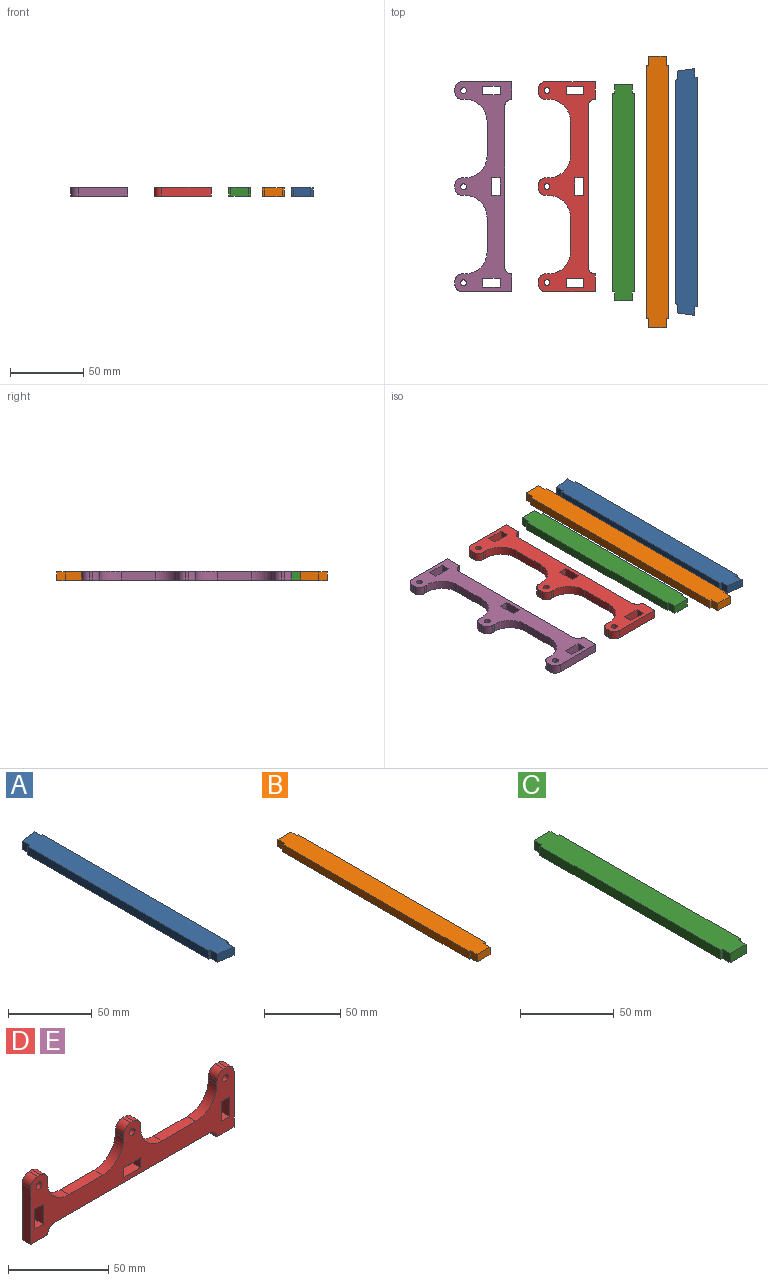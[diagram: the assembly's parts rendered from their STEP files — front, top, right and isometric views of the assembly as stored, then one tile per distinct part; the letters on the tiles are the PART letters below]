
ASSEMBLY  parts=5 mates=4
PART A: 14 faces, bbox 15x168.6x6 mm
  f0: plane 152.79x6mm, normal (-1,0,0), area 916.8mm2, adj f1,f11,f12,f13
  f1: plane 6x1.5mm, normal (-0.14,-0.99,0), area 9.1mm2, adj f0,f2,f12,f13
  f2: plane 6x6mm, normal (-1,0,0), area 36mm2, adj f1,f3,f12,f13
  f3: plane 12x6mm, normal (-0.14,-0.99,0), area 72.7mm2, adj f2,f4,f12,f13
  f4: plane 6x6mm, normal (1,0,0), area 36mm2, adj f3,f5,f12,f13
  f5: plane 6x1.5mm, normal (-0.14,-0.99,0), area 9.1mm2, adj f4,f6,f12,f13
  f6: plane 157.01x6mm, normal (1,0,0), area 942mm2, adj f5,f7,f12,f13
  f7: plane 6x1.5mm, normal (-0.14,0.99,0), area 9.1mm2, adj f6,f8,f12,f13
  f8: plane 6x6mm, normal (1,0,0), area 36mm2, adj f7,f9,f12,f13
  f9: plane 12x6mm, normal (-0.14,0.99,0), area 72.7mm2, adj f8,f10,f12,f13
  f10: plane 6x6mm, normal (-1,0,0), area 36mm2, adj f9,f11,f12,f13
  f11: plane 6x1.5mm, normal (-0.14,0.99,0), area 9.1mm2, adj f0,f10,f12,f13
  f12: plane 168.59x15mm, normal (0,0,1), area 2467.5mm2, adj f0,f1,f2,f3,f4,f5,f6,f7
  f13: plane 168.59x15mm, normal (0,0,-1), area 2467.5mm2, adj f0,f1,f2,f3,f4,f5,f6,f7
PART B: 14 faces, bbox 15x185.1x6 mm
  f0: plane 173.1x6mm, normal (-1,0,0), area 1038.6mm2, adj f1,f11,f12,f13
  f1: plane 6x1.5mm, normal (0,-1,0), area 9mm2, adj f0,f2,f12,f13
  f2: plane 6x6mm, normal (-1,0,0), area 36mm2, adj f1,f3,f12,f13
  f3: plane 12x6mm, normal (0,-1,0), area 72mm2, adj f2,f4,f12,f13
  f4: plane 6x6mm, normal (1,0,0), area 36mm2, adj f3,f5,f12,f13
  f5: plane 6x1.5mm, normal (0,-1,0), area 9mm2, adj f4,f6,f12,f13
  f6: plane 173.1x6mm, normal (1,0,0), area 1038.6mm2, adj f5,f7,f12,f13
  f7: plane 6x1.5mm, normal (0,1,0), area 9mm2, adj f6,f8,f12,f13
  f8: plane 6x6mm, normal (1,0,0), area 36mm2, adj f7,f9,f12,f13
  f9: plane 12x6mm, normal (0,1,0), area 72mm2, adj f8,f10,f12,f13
  f10: plane 6x6mm, normal (-1,0,0), area 36mm2, adj f9,f11,f12,f13
  f11: plane 6x1.5mm, normal (0,1,0), area 9mm2, adj f0,f10,f12,f13
  f12: plane 185.1x15mm, normal (0,0,1), area 2740.5mm2, adj f0,f1,f2,f3,f4,f5,f6,f7
  f13: plane 185.1x15mm, normal (0,0,-1), area 2740.5mm2, adj f0,f1,f2,f3,f4,f5,f6,f7
PART C: 14 faces, bbox 15x147.7x6 mm
  f0: plane 135.7x6mm, normal (-1,0,0), area 814.2mm2, adj f1,f11,f12,f13
  f1: plane 6x1.5mm, normal (0,-1,0), area 9mm2, adj f0,f2,f12,f13
  f2: plane 6x6mm, normal (-1,0,0), area 36mm2, adj f1,f3,f12,f13
  f3: plane 12x6mm, normal (0,-1,0), area 72mm2, adj f2,f4,f12,f13
  f4: plane 6x6mm, normal (1,0,0), area 36mm2, adj f3,f5,f12,f13
  f5: plane 6x1.5mm, normal (0,-1,0), area 9mm2, adj f4,f6,f12,f13
  f6: plane 135.7x6mm, normal (1,0,0), area 814.2mm2, adj f5,f7,f12,f13
  f7: plane 6x1.5mm, normal (0,1,0), area 9mm2, adj f6,f8,f12,f13
  f8: plane 6x6mm, normal (1,0,0), area 36mm2, adj f7,f9,f12,f13
  f9: plane 12x6mm, normal (0,1,0), area 72mm2, adj f8,f10,f12,f13
  f10: plane 6x6mm, normal (-1,0,0), area 36mm2, adj f9,f11,f12,f13
  f11: plane 6x1.5mm, normal (0,1,0), area 9mm2, adj f0,f10,f12,f13
  f12: plane 147.7x15mm, normal (0,0,1), area 2179.5mm2, adj f0,f1,f2,f3,f4,f5,f6,f7
  f13: plane 147.7x15mm, normal (0,0,-1), area 2179.5mm2, adj f0,f1,f2,f3,f4,f5,f6,f7
PART D: 43 faces, bbox 143.3x6x39 mm
  f0: cylinder r=5mm len=6mm, axis (0,1,0), area 47.1mm2, adj f1,f35,f41,f42
  f1: plane 109.26x6mm, normal (0,0,-1), area 655.6mm2, adj f0,f2,f41,f42
  f2: cylinder r=5mm len=6mm, axis (0,1,0), area 47.1mm2, adj f1,f3,f41,f42
  f3: plane 12x6mm, normal (0,0,-1), area 72mm2, adj f2,f4,f41,f42
  f4: plane 34x6mm, normal (1,0,0), area 204mm2, adj f3,f5,f41,f42
  f5: cylinder r=5mm len=6mm, axis (0,1,0), area 47.1mm2, adj f4,f6,f41,f42
  f6: plane 6x2mm, normal (0,0,1), area 12mm2, adj f5,f7,f41,f42
  f7: cylinder r=5mm len=6mm, axis (0,1,0), area 47.1mm2, adj f6,f8,f41,f42
  f8: plane 6x2mm, normal (-1,0,0), area 12mm2, adj f7,f9,f41,f42
  f9: cylinder r=15mm len=15mm, axis (0,1,0), area 141.4mm2, adj f8,f10,f41,f42
  f10: plane 23.63x6mm, normal (0,0,1), area 141.8mm2, adj f9,f11,f41,f42
  f11: cylinder r=15mm len=15mm, axis (0,1,0), area 141.4mm2, adj f10,f12,f41,f42
  f12: plane 6x2mm, normal (1,0,0), area 12mm2, adj f11,f13,f41,f42
  f13: cylinder r=5mm len=6mm, axis (0,1,0), area 47.1mm2, adj f12,f14,f41,f42
  f14: plane 6x2mm, normal (0,0,1), area 12mm2, adj f13,f15,f41,f42
  f15: cylinder r=5mm len=6mm, axis (0,1,0), area 47.1mm2, adj f14,f16,f41,f42
  f16: plane 6x2mm, normal (-1,0,0), area 12mm2, adj f15,f17,f41,f42
  f17: cylinder r=15mm len=15mm, axis (0,1,0), area 141.4mm2, adj f16,f18,f41,f42
  f18: plane 23.63x6mm, normal (0,0,1), area 141.8mm2, adj f17,f19,f41,f42
  f19: cylinder r=15mm len=15mm, axis (0,1,0), area 141.4mm2, adj f18,f20,f41,f42
  f20: plane 6x2mm, normal (1,0,0), area 12mm2, adj f19,f21,f41,f42
  f21: cylinder r=5mm len=6mm, axis (0,1,0), area 47.1mm2, adj f20,f22,f41,f42
  f22: plane 6x2mm, normal (0,0,1), area 12mm2, adj f21,f23,f41,f42
  f23: cylinder r=5mm len=6mm, axis (0,1,0), area 47.1mm2, adj f22,f24,f41,f42
  f24: plane 34x6mm, normal (-1,0,0), area 204mm2, adj f23,f35,f41,f42
  f25: plane 6x6mm, normal (0,0,-1), area 36mm2, adj f26,f36,f41,f42
  f26: plane 12x6mm, normal (-1,0,0), area 72mm2, adj f25,f27,f41,f42
  f27: plane 6x6mm, normal (0,0,1), area 36mm2, adj f26,f36,f41,f42
  f28: plane 6x6mm, normal (1,0,0), area 36mm2, adj f29,f37,f41,f42
  f29: plane 12x6mm, normal (0,0,-1), area 72mm2, adj f28,f30,f41,f42
  f30: plane 6x6mm, normal (-1,0,0), area 36mm2, adj f29,f37,f41,f42
  f31: plane 12x6mm, normal (1,0,0), area 72mm2, adj f32,f39,f41,f42
  f32: plane 6x6mm, normal (0,0,-1), area 36mm2, adj f31,f33,f41,f42
  f33: plane 12x6mm, normal (-1,0,0), area 72mm2, adj f32,f39,f41,f42
  f34: cylinder r=2mm len=6mm, axis (0,1,0), area 75.4mm2, adj f41,f42
  f35: plane 12x6mm, normal (0,0,-1), area 72mm2, adj f0,f24,f41,f42
  f36: plane 12x6mm, normal (1,0,0), area 72mm2, adj f25,f27,f41,f42
  f37: plane 12x6mm, normal (0,0,1), area 72mm2, adj f28,f30,f41,f42
  f38: cylinder r=2mm len=6mm, axis (0,1,0), area 75.4mm2, adj f41,f42
  f39: plane 6x6mm, normal (0,0,1), area 36mm2, adj f31,f33,f41,f42
  f40: cylinder r=2mm len=6mm, axis (0,1,0), area 75.4mm2, adj f41,f42
  f41: plane 143.26x39mm, normal (0,-1,0), area 2549.1mm2, adj f0,f1,f2,f3,f4,f5,f6,f7
  f42: plane 143.26x39mm, normal (0,1,0), area 2549.1mm2, adj f0,f1,f2,f3,f4,f5,f6,f7
PART E: same geometry as D
PLACE A t=(142.12,4.84,2.47)mm
PLACE B t=(122.45,4.84,2.47)mm
PLACE C t=(99.41,4.44,2.75)mm
PLACE D rot(axis=(-0.58,-0.58,0.58),120deg) t=(80.07,8.51,2.75)mm
PLACE E rot(axis=(-0.58,-0.58,0.58),120deg) t=(23.07,8.51,2.75)mm
MATE parallel E.f41 <-> C.f12  axis (0,0,1) through (18.07,63.14,8.75)mm
MATE parallel A.f12 <-> B.f12  axis (0,0,1) through (142.15,4.84,8.47)mm
MATE parallel A.f12 <-> C.f12  axis (0,0,1) through (142.15,4.84,8.47)mm
MATE parallel D.f41 <-> E.f41  axis (0,0,1) through (75.07,63.14,8.75)mm
